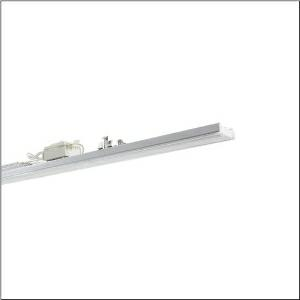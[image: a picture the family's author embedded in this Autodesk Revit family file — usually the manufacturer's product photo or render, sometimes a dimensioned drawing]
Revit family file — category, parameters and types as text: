
# Revit family: licross_r__11_recessed_mo_51tl14dn38xg_a982
name_source: partatom
category: Lighting Fixtures
units: mm (PartAtom-declared; Revit-internal decimal feet)

## family parameters
Cut with Voids When Loaded = No
Host = Face
Light Source = No
Part Type = Normal
Room Calculation Point = No
Round Connector Dimension = Use Diameter
Shared = No

## types (1)
- --- (1 x LED, 8040 lm, 49.7 W, 3000K)
    Apparent Load = 50 VA
    CIE Flux Codes = 56 84 97 100 100
    Color Rendering = 80
    Color Temperature = 3000K
    Default Elevation = 1800 mm
    Description = Licross® 11 Recessed MO, luminaire insert, of sheet steel, coil coated, white, length: 1.500mm, width: 66mm, height: 67mm, LED rated luminous flux: 8.040lm, light colour: 830, control gear: DALI 2, with plug, 5-pole, with phase selection, mains connection: 220..240V, AC, 50/60Hz, rated input power: 49.7W, halogen-free wiring, primary light control with lens, of plastic, primary optical cover: cover, of PMMA, light emission: direct distribution, primary light characteristic: asymmetric, protection rating (complete): IP40, insulation class (complete): insulation class I (protective earthing), certification: CE, ENEC, VDE, UKCA, protection symbol: D if used in an environment without relevant dust loads with corresponding accessories, impact resistance: IK06, permissible ambient temperature for indoor applications: -25..+35°C, corresponds to IFS (International Featured Standards) requirements for safety and quality in the food industry, reducing of maximum allowable ambient temperature of 5°C with ceiling mounting, LABS conformity tested according to VDMA 24364:2018-05, packaging unit: 1 piece
    Height = 58 mm
    Lamp = 1 x LED
    Lamp Light Flux = 8040 lm
    Lamp Power = 49.7 W
    Lamp count = 1
    Length = 1500 mm
    Luminous efficacy = 162 lm/W
    Manufacturer = Siteco
    ModVariant = No
    Model = 51TL14DN38XG
    Mounting Place = Ceiling
    Mounting Type = Pendant
    Number of Poles = 1
    OnlyDefault = Yes
    Power Factor = 1
    Product Name = Licross® 11 Recessed MO
    Product group = luminaire insert
    ProductGroupID = 902
    Protection Class = Protection class I
    Protection Degree = IP 40
    RLX_Detail_Level = 1
    RLX_Emergency_Light_Flux = 0 lm
    RLX_Emergency_Type = 0
    RLX_Emergency_Type_DB = No
    RlxData = <blob elided: 25073 chars, md5=473374a2>
    Socket = socket
    Standby Power = 0 W
    System Light Flux = 8040 lm
    System Power = 50 W
    Type Comments = factory setting: luminous flux: 100 % | dim-lin: 254 | 332 mA
    Type Image = l_1296930.jpg
    URL = http://relux.com
    VarID = @adj_031470
    Voltage = 0 V
    Weight = 0.00 kg
    Width = 66 mm

## geometry (parser evidence)
native form markers: Blend x4, Sweep x9
no freeform markers — native parametric forms only
